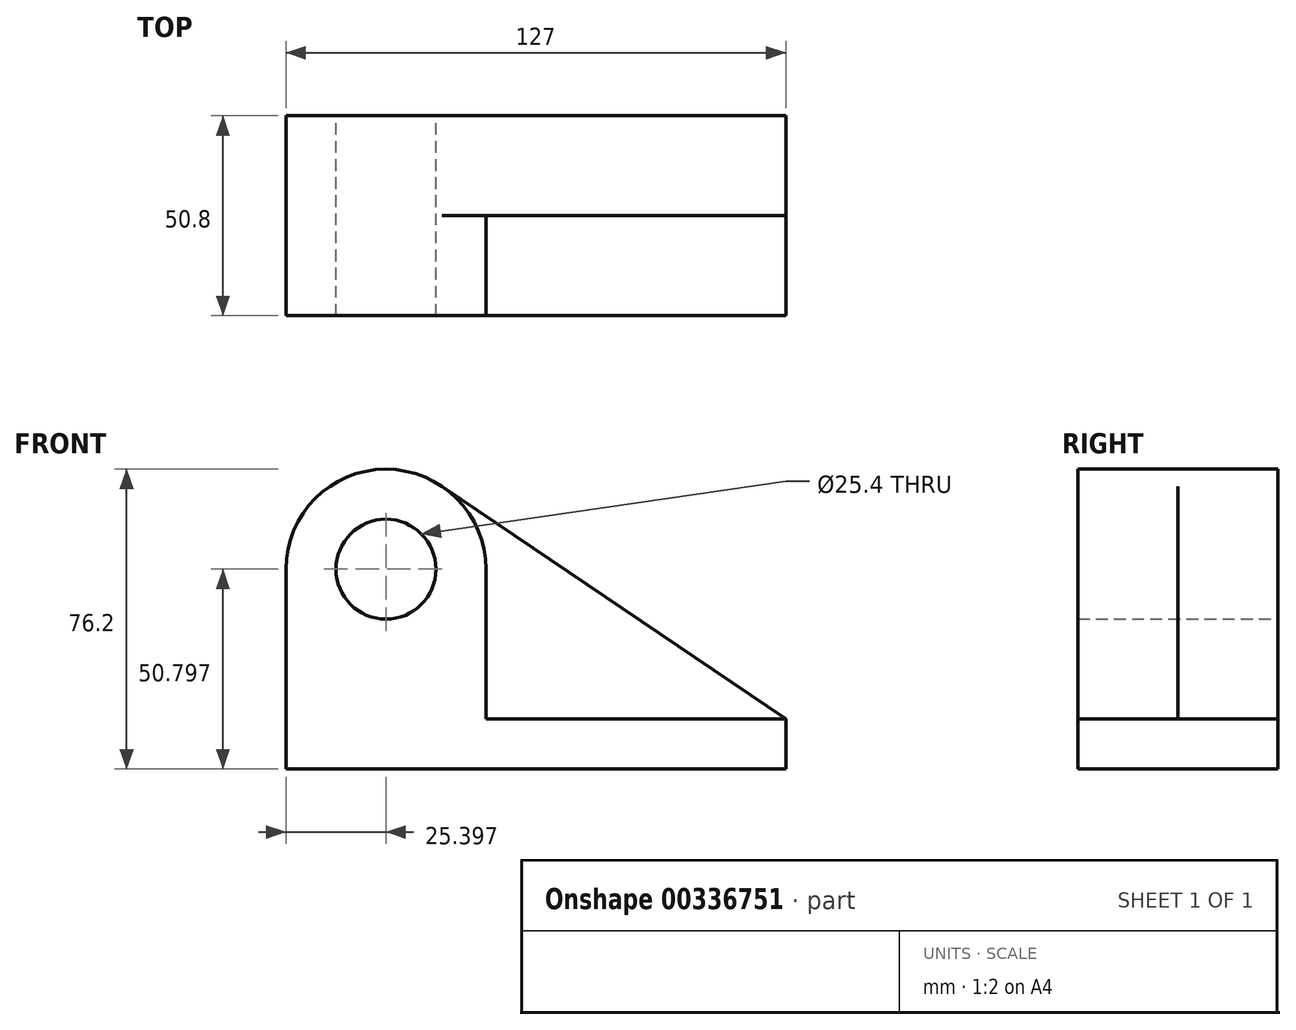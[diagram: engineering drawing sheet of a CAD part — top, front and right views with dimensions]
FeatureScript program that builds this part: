
annotation { "Feature Type Name" : "Feature", "Feature Type Description" : "" }
export const myFeature = defineFeature(function(context is Context, id is Id, definition is map)
    precondition{}
    {
        {
            var Q0;
            Q0=qCreatedBy(makeId("Front.planeOp"),FACE);
            var sketch = newSketch(context, id + "F0", { "sketchPlane" : qUnion([Q0])});
            skCircle(sketch, "E0", {"center": v(-41.45, 36.02) * mm, "radius": 12.7 * mm});
            skArc(sketch, "E1", {"start": v(-27.21, 57.05) * mm, "mid": v(-53.36, 58.45) * mm, "end": v(-66.85, 36.02) * mm});
            skLineSegment(sketch, "E2", {"start": v(-66.85, 36.02) * mm, "end": v(-66.85, -14.78) * mm});
            skLineSegment(sketch, "E3", {"start": v(-66.85, -14.78) * mm, "end": v(60.15, -14.78) * mm});
            skLineSegment(sketch, "E4", {"start": v(60.15, -14.78) * mm, "end": v(60.15, -2.08) * mm});
            skLineSegment(sketch, "E5", {"start": v(60.15, -2.08) * mm, "end": v(-27.21, 57.05) * mm});
            skSolve(sketch);
        }
        {
            var Q0;
            Q0=makeQuery(id+"F0.imprint","IMPRINT",FACE,{"disambiguationData":[TD([[makeQuery(id+"F0.imprint","IMPRINT",EDGE,{"derivedFrom":sQuery(id+"F0.wireOp",EDGE,"E0")}),-1.0]])]});
            extrude(context, id + "F1", {"entities" : qUnion([Q0]), "depth" : 25.4 * mm});
        }
        {
            var Q0;
            Q0=makeQuery(id+"F1.opExtrude","CAP_FACE",FACE,{"disambiguationData":[OSD([sQuery(id+"F0.wireOp",EDGE,"E0"),sQuery(id+"F0.wireOp",EDGE,"E1"),sQuery(id+"F0.wireOp",EDGE,"E2"),sQuery(id+"F0.wireOp",EDGE,"E3"),sQuery(id+"F0.wireOp",EDGE,"E4"),sQuery(id+"F0.wireOp",EDGE,"E5")])],"isStart":false});
            var sketch = newSketch(context, id + "F2", { "sketchPlane" : qUnion([Q0])});
            skCircle(sketch, "E6", {"center": v(-41.45, 36.02) * mm, "radius": 12.7 * mm});
            skLineSegment(sketch, "E7.bottom", {"start": v(60.15, -2.08) * mm, "end": v(-16.05, -2.08) * mm});
            skLineSegment(sketch, "E7.top", {"start": v(60.15, -14.78) * mm, "end": v(-66.85, -14.78) * mm});
            skLineSegment(sketch, "E7.left", {"start": v(60.15, -2.08) * mm, "end": v(60.15, -14.78) * mm});
            skLineSegment(sketch, "E7.right", {"start": v(-66.85, -2.08) * mm, "end": v(-66.85, -14.78) * mm});
            skArc(sketch, "E8", {"start": v(-16.05, 36.02) * mm, "mid": v(-41.45, 61.42) * mm, "end": v(-66.85, 36.02) * mm});
            skLineSegment(sketch, "E9", {"start": v(-41.45, 36.02) * mm, "end": v(-16.05, 36.02) * mm});
            skLineSegment(sketch, "E10", {"start": v(-16.05, 36.02) * mm, "end": v(-16.05, -2.08) * mm});
            skLineSegment(sketch, "E11", {"start": v(-41.45, 36.02) * mm, "end": v(-66.85, 36.02) * mm});
            skLineSegment(sketch, "E12", {"start": v(-66.85, 36.02) * mm, "end": v(-66.85, -2.08) * mm});
            skSolve(sketch);
        }
        {
            var Q0;
            Q0=makeQuery(id+"F2.imprint","IMPRINT",FACE,{"disambiguationData":[TD([[makeQuery(id+"F2.imprint","IMPRINT",EDGE,{"derivedFrom":sQuery(id+"F2.wireOp",EDGE,"E7.bottom")}),1.0]])]});
            var Q1;
            {var subQ2=sQuery(id+"F2.wireOp",EDGE,"E9");var subQ4=sQuery(id+"F2.wireOp",EDGE,"E6");var subQ5=makeQuery(id+"F2.imprint","INTERSECT",VERTEX,{"derivedFrom":[subQ4,subQ2]});Q1=makeQuery(id+"F2.imprint","IMPRINT",FACE,{"disambiguationData":[TD([[makeQuery(id+"F2.imprint","IMPRINT",EDGE,{"disambiguationData":[TD([[subQ5,-1.0]])],"derivedFrom":subQ4}),-1.0]])]});}
            extrude(context, id + "F3", {"entities" : qUnion([Q0, Q1]), "operationType" : NewBodyOperationType.ADD, "depth" : 25.4 * mm});
        }
    });
